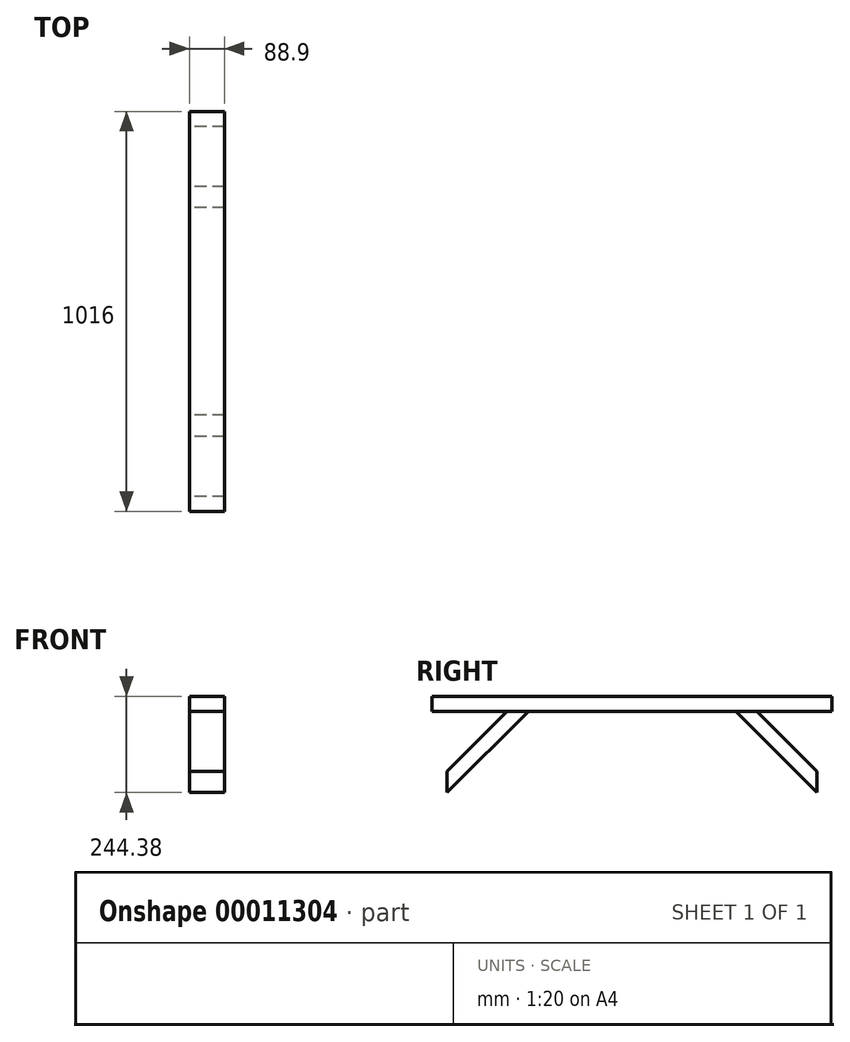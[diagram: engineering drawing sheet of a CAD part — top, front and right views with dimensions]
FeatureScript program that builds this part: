
annotation { "Feature Type Name" : "Feature", "Feature Type Description" : "" }
export const myFeature = defineFeature(function(context is Context, id is Id, definition is map)
    precondition{}
    {
        {
            var Q0;
            Q0=qCreatedBy(makeId("Front.planeOp"),FACE);
            var sketch = newSketch(context, id + "F0", { "sketchPlane" : qUnion([Q0])});
            skLineSegment(sketch, "E0.bottom", {"start": v(0, 0) * mm, "end": v(88.9, 0) * mm});
            skLineSegment(sketch, "E0.top", {"start": v(0, 38.1) * mm, "end": v(88.9, 38.1) * mm});
            skLineSegment(sketch, "E0.left", {"start": v(0, 0) * mm, "end": v(0, 38.1) * mm});
            skLineSegment(sketch, "E0.right", {"start": v(88.9, 0) * mm, "end": v(88.9, 38.1) * mm});
            skSolve(sketch);
        }
        {
            var Q0;
            Q0=makeQuery(id+"F0.imprint","IMPRINT",FACE,{"disambiguationData":[TD([[makeQuery(id+"F0.imprint","IMPRINT",EDGE,{"derivedFrom":sQuery(id+"F0.wireOp",EDGE,"E0.bottom")}),1.0]])]});
            extrude(context, id + "F1", {"entities" : qUnion([Q0]), "oppositeDirection" : true, "depth" : 1016 * mm});
        }
        {
            var Q0;
            Q0=makeQuery(id+"F1.opExtrude","SWEPT_FACE",FACE,{"disambiguationData":[OSD([sQuery(id+"F0.wireOp",EDGE,"E0.left")])]});
            var sketch = newSketch(context, id + "F2", { "sketchPlane" : qUnion([Q0])});
            skLineSegment(sketch, "E1", {"start": v(0, 0) * mm, "end": v(-38.1, 0) * mm, "construction": true});
            skLineSegment(sketch, "E2", {"start": v(-38.1, 0) * mm, "end": v(-190.5, 0) * mm, "construction": true});
            skLineSegment(sketch, "E3", {"start": v(-190.5, 0) * mm, "end": v(-38.1, -152.4) * mm});
            skLineSegment(sketch, "E4", {"start": v(-38.1, -152.4) * mm, "end": v(-38.1, -206.28) * mm});
            skLineSegment(sketch, "E5", {"start": v(-38.1, -206.28) * mm, "end": v(-244.38, 0) * mm});
            skLineSegment(sketch, "E6", {"start": v(-244.38, 0) * mm, "end": v(-190.5, 0) * mm});
            skLineSegment(sketch, "E7", {"start": v(-38.1, 0) * mm, "end": v(-38.1, -152.4) * mm, "construction": true});
            skSolve(sketch);
        }
        {
            var Q0;
            Q0 = qSketchRegion(id + "F2", true);
            var Q1;
            Q1=makeQuery(id+"F1.opExtrude","SWEPT_FACE",FACE,{"disambiguationData":[OSD([sQuery(id+"F0.wireOp",EDGE,"E0.right")])]});
            extrude(context, id + "F3", {"entities" : qUnion([Q0]), "endBound" : BoundingType.UP_TO_SURFACE, "oppositeDirection" : true, "endBoundEntityFace" : qUnion([Q1]), "depth" : 25.4 * mm});
        }
        {
            var Q0;
            Q0=makeQuery(id+"F1.opExtrude","SWEPT_FACE",FACE,{"disambiguationData":[OSD([sQuery(id+"F0.wireOp",EDGE,"E0.right")])]});
            var sketch = newSketch(context, id + "F4", { "sketchPlane" : qUnion([Q0])});
            skLineSegment(sketch, "E8", {"start": v(508, 38.1) * mm, "end": v(508, 0) * mm});
            skSolve(sketch);
        }
        {
            var Q0;
            Q0=makeQuery(id+"F1.opExtrude","SWEPT_FACE",FACE,{"disambiguationData":[OSD([sQuery(id+"F0.wireOp",EDGE,"E0.top")])]});
            var sketch = newSketch(context, id + "F5", { "sketchPlane" : qUnion([Q0])});
            skPoint(sketch, "E9", {"position": v(0, 508) * mm});
            skPoint(sketch, "E10", {"position": v(88.9, 508) * mm});
            skSolve(sketch);
        }
        {
            var Q0;
            Q0=sQuery(id+"F5.wireOp",VERTEX,"E9");
            var Q1;
            Q1=sQuery(id+"F5.wireOp",VERTEX,"E10");
            var Q2;
            Q2=sQuery(id+"F4.wireOp",VERTEX,"E8.end");
            cPlane(context, id + "F6", {"entities" : qUnion([Q0, Q1, Q2]), "cplaneType" : CPlaneType.THREE_POINT, "offset" : 0 * mm, "width" : 152.4 * mm, "height" : 152.4 * mm});
        }
        {
            var Q0;
            Q0=makeQuery(id+"F3.opExtrude","SWEPT_BODY",BODY,{"disambiguationData":[OSD([sQuery(id+"F2.wireOp",EDGE,"E3"),sQuery(id+"F2.wireOp",EDGE,"E4"),sQuery(id+"F2.wireOp",EDGE,"E5"),sQuery(id+"F2.wireOp",EDGE,"E6")])]});
            var Q1;
            Q1=qCreatedBy(id+"F6.planeOp",FACE);
            mirror(context, id + "F7", {"entities" : qUnion([Q0]), "mirrorPlane" : qUnion([Q1])});
        }
    });
